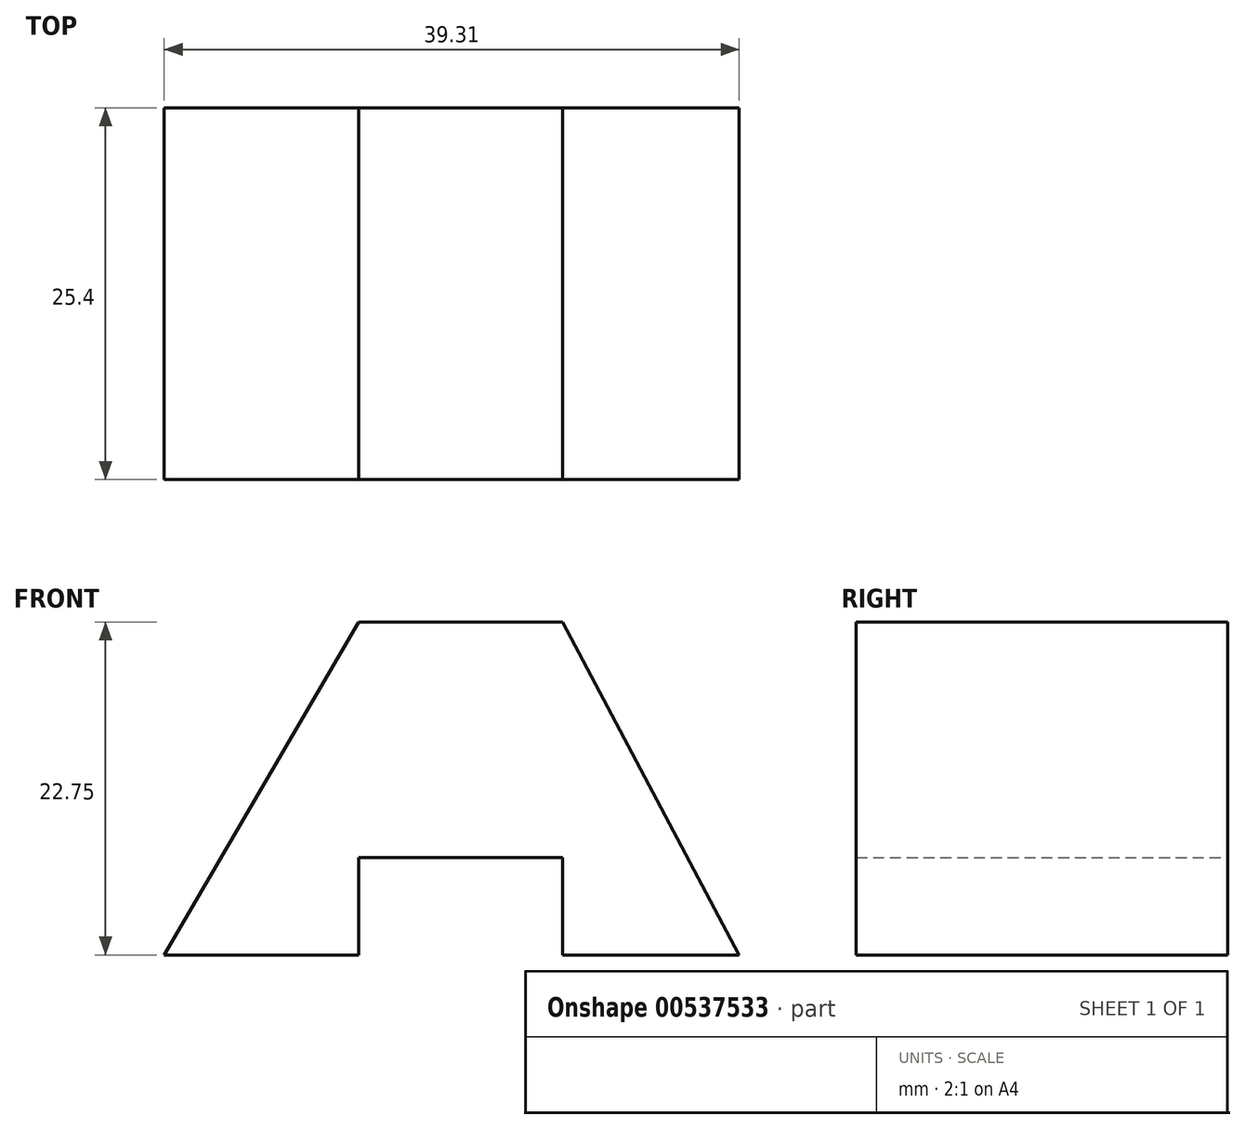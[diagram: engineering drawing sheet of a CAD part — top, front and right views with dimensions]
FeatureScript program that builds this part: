
annotation { "Feature Type Name" : "Feature", "Feature Type Description" : "" }
export const myFeature = defineFeature(function(context is Context, id is Id, definition is map)
    precondition{}
    {
        {
            var Q0;
            Q0=qCreatedBy(makeId("Front.planeOp"),FACE);
            var sketch = newSketch(context, id + "F0", { "sketchPlane" : qUnion([Q0])});
            skLineSegment(sketch, "E0", {"start": v(0, 0) * mm, "end": v(13.3, 0) * mm});
            skLineSegment(sketch, "E1", {"start": v(13.3, 0) * mm, "end": v(13.3, 6.65) * mm});
            skLineSegment(sketch, "E2", {"start": v(13.3, 6.65) * mm, "end": v(27.24, 6.65) * mm});
            skLineSegment(sketch, "E3", {"start": v(27.24, 6.65) * mm, "end": v(27.24, 0) * mm});
            skLineSegment(sketch, "E4", {"start": v(27.24, 0) * mm, "end": v(39.3, 0) * mm});
            skLineSegment(sketch, "E5", {"start": v(39.3, 0) * mm, "end": v(27.24, 22.75) * mm});
            skLineSegment(sketch, "E6", {"start": v(27.24, 22.75) * mm, "end": v(13.3, 22.75) * mm});
            skLineSegment(sketch, "E7", {"start": v(13.3, 22.75) * mm, "end": v(0, 0) * mm});
            skSolve(sketch);
        }
        {
            var Q0;
            Q0 = qSketchRegion(id + "F0", true);
            extrude(context, id + "F1", {"entities" : qUnion([Q0]), "depth" : 25.4 * mm, "offsetDistance" : 25.4 * mm});
        }
    });
